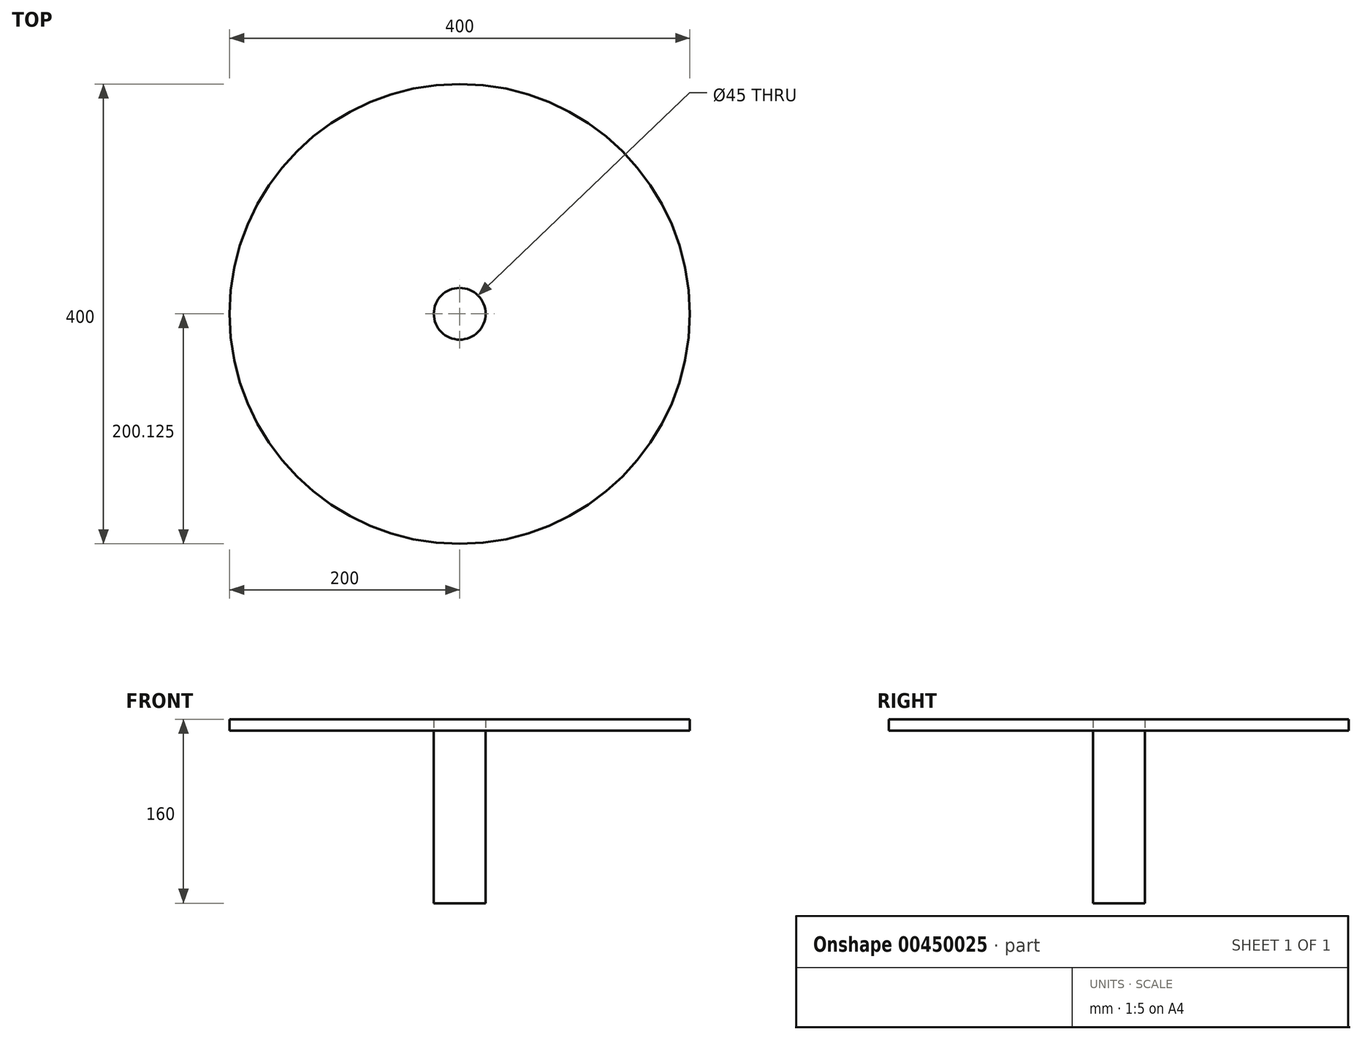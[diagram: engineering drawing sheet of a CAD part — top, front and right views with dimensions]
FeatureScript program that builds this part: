
annotation { "Feature Type Name" : "Feature", "Feature Type Description" : "" }
export const myFeature = defineFeature(function(context is Context, id is Id, definition is map)
    precondition{}
    {
        {
            var Q0;
            Q0=qCreatedBy(makeId("Top.planeOp"),FACE);
            var sketch = newSketch(context, id + "F0", { "sketchPlane" : qUnion([Q0])});
            skCircle(sketch, "E0", {"center": v(0, 0.13) * mm, "radius": 22.5 * mm});
            skSolve(sketch);
        }
        {
            var Q0;
            Q0=makeQuery(id+"F0.imprint","IMPRINT",FACE,{"disambiguationData":[TD([[makeQuery(id+"F0.imprint","IMPRINT",EDGE,{"derivedFrom":sQuery(id+"F0.wireOp",EDGE,"E0")}),1.0]])]});
            extrude(context, id + "F1", {"entities" : qUnion([Q0]), "depth" : 150 * mm});
        }
        {
            var Q0;
            Q0=makeQuery(id+"F1.opExtrude","CAP_FACE",FACE,{"disambiguationData":[OSD([sQuery(id+"F0.wireOp",EDGE,"E0")])],"isStart":false});
            var sketch = newSketch(context, id + "F2", { "sketchPlane" : qUnion([Q0])});
            skCircle(sketch, "E1", {"center": v(0, 0) * mm, "radius": 200 * mm});
            skSolve(sketch);
        }
        {
            var Q0;
            Q0=makeQuery(id+"F2.imprint","IMPRINT",FACE,{"disambiguationData":[TD([[makeQuery(id+"F2.imprint","IMPRINT",EDGE,{"derivedFrom":sQuery(id+"F2.wireOp",EDGE,"E1")}),1.0]])]});
            extrude(context, id + "F3", {"entities" : qUnion([Q0]), "depth" : 10 * mm});
        }
    });
